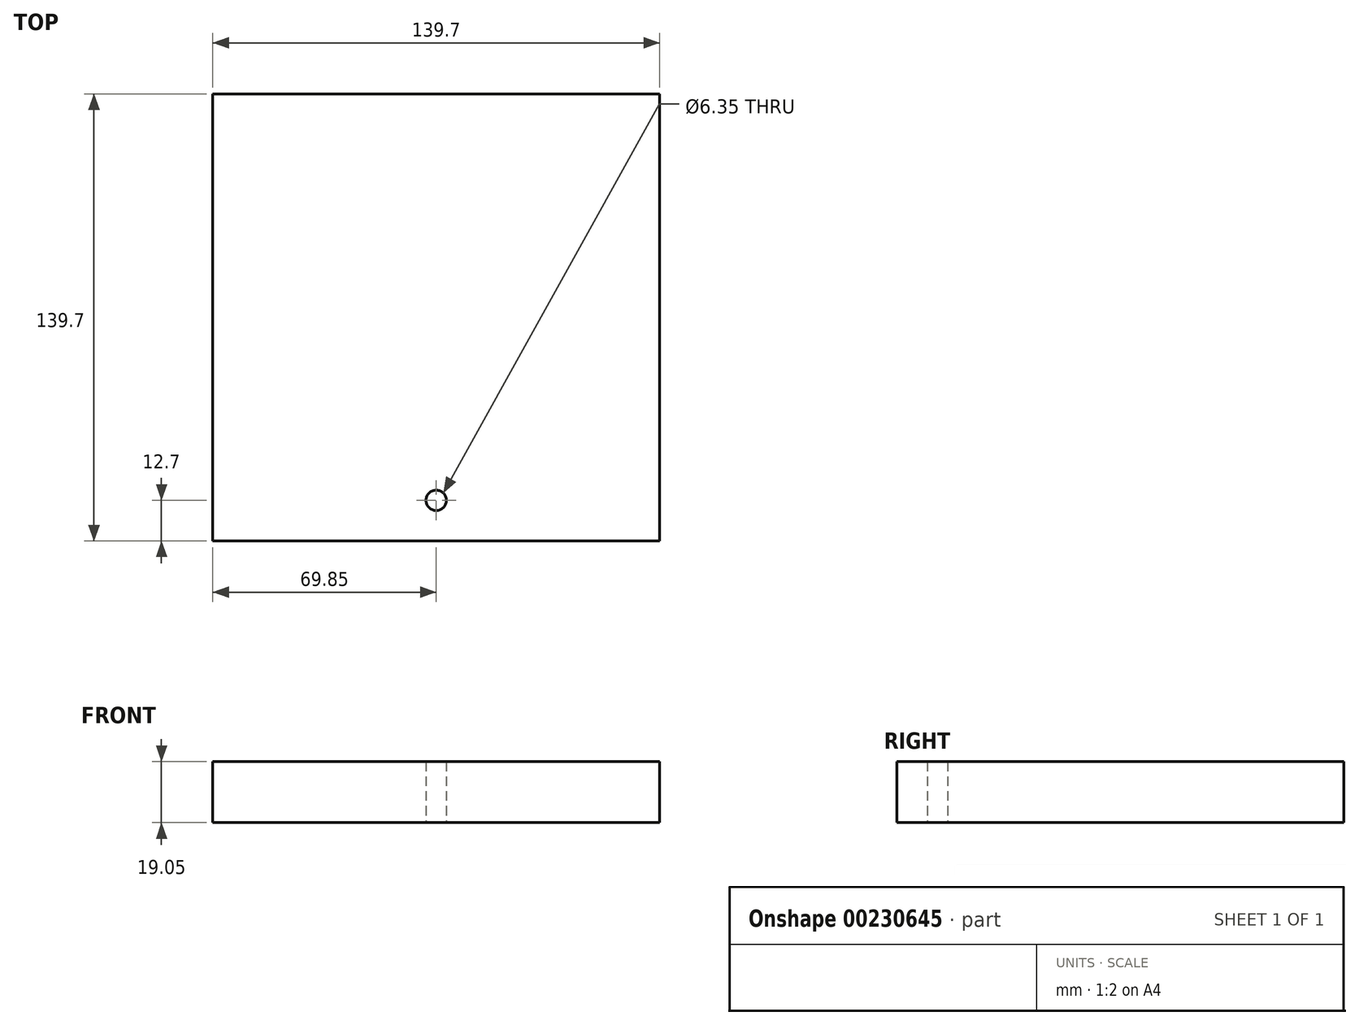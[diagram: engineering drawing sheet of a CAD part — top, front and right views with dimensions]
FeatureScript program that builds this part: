
annotation { "Feature Type Name" : "Feature", "Feature Type Description" : "" }
export const myFeature = defineFeature(function(context is Context, id is Id, definition is map)
    precondition{}
    {
        {
            var Q0;
            Q0=qCreatedBy(makeId("Top.planeOp"),FACE);
            var sketch = newSketch(context, id + "F0", { "sketchPlane" : qUnion([Q0])});
            skLineSegment(sketch, "E0.bottom", {"start": v(69.85, 69.85) * mm, "end": v(-69.85, 69.85) * mm});
            skLineSegment(sketch, "E0.top", {"start": v(69.85, -69.85) * mm, "end": v(-69.85, -69.85) * mm});
            skLineSegment(sketch, "E0.left", {"start": v(69.85, 69.85) * mm, "end": v(69.85, -69.85) * mm});
            skLineSegment(sketch, "E0.right", {"start": v(-69.85, 69.85) * mm, "end": v(-69.85, -69.85) * mm});
            skPoint(sketch, "E0.middle", {"position": v(0, 0) * mm});
            skLineSegment(sketch, "E1", {"start": v(0, -69.85) * mm, "end": v(0, -57.15) * mm});
            skPoint(sketch, "E1.endSnap0", {"position": v(0, -69.85) * mm});
            skCircle(sketch, "E2", {"center": v(0, -57.15) * mm, "radius": 3.18 * mm});
            skSolve(sketch);
        }
        {
            var Q0;
            Q0=makeQuery(id+"F0.imprint","IMPRINT",FACE,{"disambiguationData":[TD([[makeQuery(id+"F0.imprint","IMPRINT",EDGE,{"derivedFrom":sQuery(id+"F0.wireOp",EDGE,"E0.bottom")}),1.0]])]});
            extrude(context, id + "F1", {"entities" : qUnion([Q0]), "depth" : 19.05 * mm});
        }
    });
